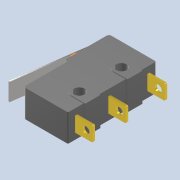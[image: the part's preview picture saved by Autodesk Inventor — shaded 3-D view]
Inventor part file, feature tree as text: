
AUTODESK INVENTOR PART (.ipt)
format: ipt  version: 2020.2 (Build 242310000, 310)  size: 253,952 bytes
history: native  units: mm
features: extrude x8, sketch x8, other x5, fillet x3, projected_geometry x1
ambient origin geometry x8: Origin, YZ Plane, XZ Plane, XY Plane, X Axis, Y Axis, Z Axis, Center Point
bodies: Body1 (feature_tree)
feature tree (25):
  other  "實體1"
  extrude  "擠出1"  Depth=10.65mm
  extrude  "擠出2"  Depth=19.9mm
  extrude  "擠出3"  Depth=6.16mm TaperAngle=0.0deg
  extrude  "擠出4"  Depth=10.0mm
  extrude  "擠出5"  TaperAngle=0.0deg  [1 undecoded]
  extrude  "擠出6"  Depth=0.4mm
  extrude  "擠出7"  Depth=4.75mm
  extrude  "擠出8"  Depth=6.48mm TaperAngle=0.0deg
  fillet  "圓角1"  Radius=9.5mm
  fillet  "圓角2"  Radius=3.4mm
  fillet  "圓角3"  Radius=3.5mm
  sketch  "草圖1"
  sketch  "草圖2"
  sketch  "草圖3"
  sketch  "草圖4"
  projected_geometry  "投影迴路1"
  sketch  "草圖5"
  sketch  "草圖6"
  sketch  "草圖7"
  sketch  "草圖8"
  other  "投影切割邊1"
  other  "投影切割邊2"
  other  "投影切割邊3"
  other  "投影切割邊4"
note: 1 required parameter value undecoded (feature->parameter linkage not recoverable at this tier; creation-order binding heuristic only, values carry confidence <= 0.55)
